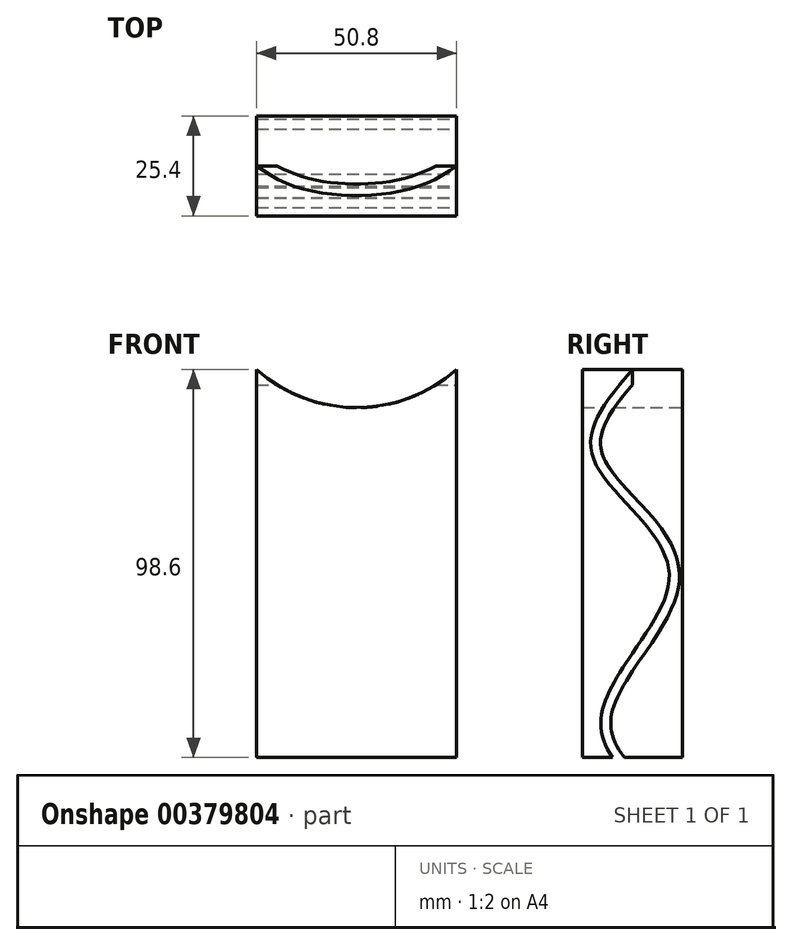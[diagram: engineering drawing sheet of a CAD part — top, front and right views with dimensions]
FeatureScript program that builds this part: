
annotation { "Feature Type Name" : "Feature", "Feature Type Description" : "" }
export const myFeature = defineFeature(function(context is Context, id is Id, definition is map)
    precondition{}
    {
        {
            var Q0;
            Q0=qCreatedBy(makeId("Top.planeOp"),FACE);
            var sketch = newSketch(context, id + "F0", { "sketchPlane" : qUnion([Q0])});
            skLineSegment(sketch, "E0", {"start": v(0, 0) * mm, "end": v(50.8, 0) * mm});
            skLineSegment(sketch, "E1", {"start": v(50.8, 0) * mm, "end": v(50.8, 25.4) * mm});
            skLineSegment(sketch, "E2", {"start": v(50.8, 25.4) * mm, "end": v(0, 25.4) * mm});
            skLineSegment(sketch, "E3", {"start": v(0, 25.4) * mm, "end": v(0, 0) * mm});
            skSolve(sketch);
        }
        {
            var Q0;
            Q0=makeQuery(id+"F0.imprint","IMPRINT",FACE,{"disambiguationData":[TD([[makeQuery(id+"F0.imprint","IMPRINT",EDGE,{"derivedFrom":sQuery(id+"F0.wireOp",EDGE,"E0")}),1.0]])]});
            extrude(context, id + "F1", {"entities" : qUnion([Q0]), "depth" : 127 * mm});
        }
        {
            var Q0;
            Q0=makeQuery(id+"F1.opExtrude","SWEPT_FACE",FACE,{"disambiguationData":[OSD([sQuery(id+"F0.wireOp",EDGE,"E2")])]});
            var sketch = newSketch(context, id + "F2", { "sketchPlane" : qUnion([Q0])});
            skCircle(sketch, "E4", {"center": v(-25.4, 127) * mm, "radius": 38.1 * mm});
            skSolve(sketch);
        }
        {
            var Q0;
            {var subQ1=sQuery(id+"F0.wireOp",EDGE,"E2");var subQ6=makeQuery(id+"F1.opExtrude","CAP_EDGE",EDGE,{"disambiguationData":[OSD([subQ1])],"isStart":false});Q0=makeQuery(id+"F2.imprint","IMPRINT",FACE,{"disambiguationData":[TD([[makeQuery(id+"F2.imprint","IMPRINT",EDGE,{"derivedFrom":subQ6}),-1.0]])]});}
            extrude(context, id + "F3", {"entities" : qUnion([Q0]), "operationType" : NewBodyOperationType.REMOVE, "oppositeDirection" : true, "depth" : 99.57 * mm});
        }
        {
            var Q0;
            Q0=makeQuery(id+"F1.opExtrude","SWEPT_FACE",FACE,{"disambiguationData":[OSD([sQuery(id+"F0.wireOp",EDGE,"E1")])]});
            var sketch = newSketch(context, id + "F4", { "sketchPlane" : qUnion([Q0])});
            skLineSegment(sketch, "E5", {"start": v(12.7, 98.6) * mm, "end": v(12.7, 0) * mm});
            skFitSpline(sketch, "E6", {"points": [v(12.7, 98.6) * mm, v(2.67, 76.23) * mm, v(22.07, 46.47) * mm, v(4.68, 8.02) * mm, v(24.74, -21.73) * mm, v(12.7, -42.12) * mm], "startDerivative": vector(-107.98, -126.46) * mm, "endDerivative": vector(-123.9, -115.22) * mm});
            skFitSpline(sketch, "E7.0", {"points": [v(14.63, 96.95) * mm, v(13.5, 95.64) * mm, v(11.28, 93.03) * mm, v(8.32, 89.21) * mm, v(6.43, 86.14) * mm, v(5.38, 83.8) * mm, v(4.86, 82.12) * mm, v(4.6, 80.5) * mm, v(4.61, 79.2) * mm, v(4.77, 78.17) * mm, v(4.96, 77.38) * mm, v(5.23, 76.59) * mm, v(5.6, 75.75) * mm, v(6.08, 74.87) * mm, v(6.82, 73.66) * mm, v(8.42, 71.43) * mm, v(11.37, 68.05) * mm, v(15.4, 63.75) * mm, v(18.7, 59.94) * mm, v(21.03, 56.7) * mm, v(22.54, 54.17) * mm, v(23.53, 51.94) * mm, v(24.1, 50.08) * mm, v(24.42, 48.64) * mm, v(24.6, 47.16) * mm, v(24.63, 45.65) * mm, v(24.5, 44.17) * mm, v(24.16, 42.2) * mm, v(23.44, 39.8) * mm, v(22.22, 36.96) * mm, v(20.74, 34.18) * mm, v(18.52, 30.51) * mm, v(15.44, 26) * mm, v(12.44, 21.58) * mm, v(10.38, 18.17) * mm, v(9.07, 15.68) * mm, v(8.06, 13.3) * mm, v(7.4, 11.05) * mm, v(7.2, 9.48) * mm, v(7.2, 8.49) * mm, v(7.23, 7.83) * mm, v(7.37, 6.7) * mm, v(7.83, 5.02) * mm, v(8.76, 2.95) * mm, v(10.05, 0.84) * mm, v(12.15, -2.02) * mm, v(15.34, -5.61) * mm, v(18.79, -9.18) * mm, v(21.42, -12.04) * mm, v(23.26, -14.19) * mm, v(24.63, -16) * mm, v(25.59, -17.5) * mm, v(26.23, -18.64) * mm, v(26.77, -19.82) * mm, v(27.2, -21.03) * mm, v(27.5, -22.27) * mm, v(27.72, -23.93) * mm, v(27.66, -25.96) * mm, v(27.11, -28.3) * mm, v(26.2, -30.52) * mm, v(24.59, -33.32) * mm, v(22, -36.6) * mm, v(18.33, -40.36) * mm, v(15.72, -42.78) * mm, v(14.43, -43.98) * mm]});
            skLineSegment(sketch, "E8", {"start": v(12.7, 98.6) * mm, "end": v(14.63, 96.95) * mm});
            skLineSegment(sketch, "E9", {"start": v(12.7, -42.12) * mm, "end": v(14.43, -43.98) * mm});
            skSolve(sketch);
        }
        {
            var Q0;
            {var subQ0=sQuery(id+"F4.wireOp",EDGE,"E7.0");var subQ1=sQuery(id+"F4.wireOp",EDGE,"E5");var subQ2=makeQuery(id+"F4.imprint","INTERSECT",VERTEX,{"disambiguationData":[OD(1.0)],"derivedFrom":[subQ1,subQ0]});Q0=makeQuery(id+"F4.imprint","IMPRINT",FACE,{"disambiguationData":[TD([[makeQuery(id+"F4.imprint","IMPRINT",EDGE,{"disambiguationData":[TD([[subQ2,-1.0]])],"derivedFrom":subQ1}),1.0]])]});}
            var Q1;
            {var subQ0=sQuery(id+"F4.wireOp",EDGE,"E6");var subQ1=sQuery(id+"F4.wireOp",EDGE,"E5");var subQ2=makeQuery(id+"F4.imprint","INTERSECT",VERTEX,{"disambiguationData":[OD(1.0)],"derivedFrom":[subQ1,subQ0]});Q1=makeQuery(id+"F4.imprint","IMPRINT",FACE,{"disambiguationData":[TD([[makeQuery(id+"F4.imprint","IMPRINT",EDGE,{"disambiguationData":[TD([[subQ2,-1.0]])],"derivedFrom":subQ1}),-1.0]])]});}
            var Q2;
            {var subQ1=sQuery(id+"F4.wireOp",EDGE,"E5");var subQ3=sQuery(id+"F4.wireOp",EDGE,"E7.0");var subQ5=makeQuery(id+"F4.imprint","INTERSECT",VERTEX,{"disambiguationData":[OD(1.0)],"derivedFrom":[subQ1,subQ3]});Q2=makeQuery(id+"F4.imprint","IMPRINT",FACE,{"disambiguationData":[TD([[makeQuery(id+"F4.imprint","IMPRINT",EDGE,{"disambiguationData":[TD([[subQ5,-1.0]])],"derivedFrom":subQ1}),-1.0]])]});}
            extrude(context, id + "F5", {"entities" : qUnion([Q0, Q1, Q2]), "operationType" : NewBodyOperationType.REMOVE, "oppositeDirection" : true, "depth" : 87.63 * mm});
        }
    });
